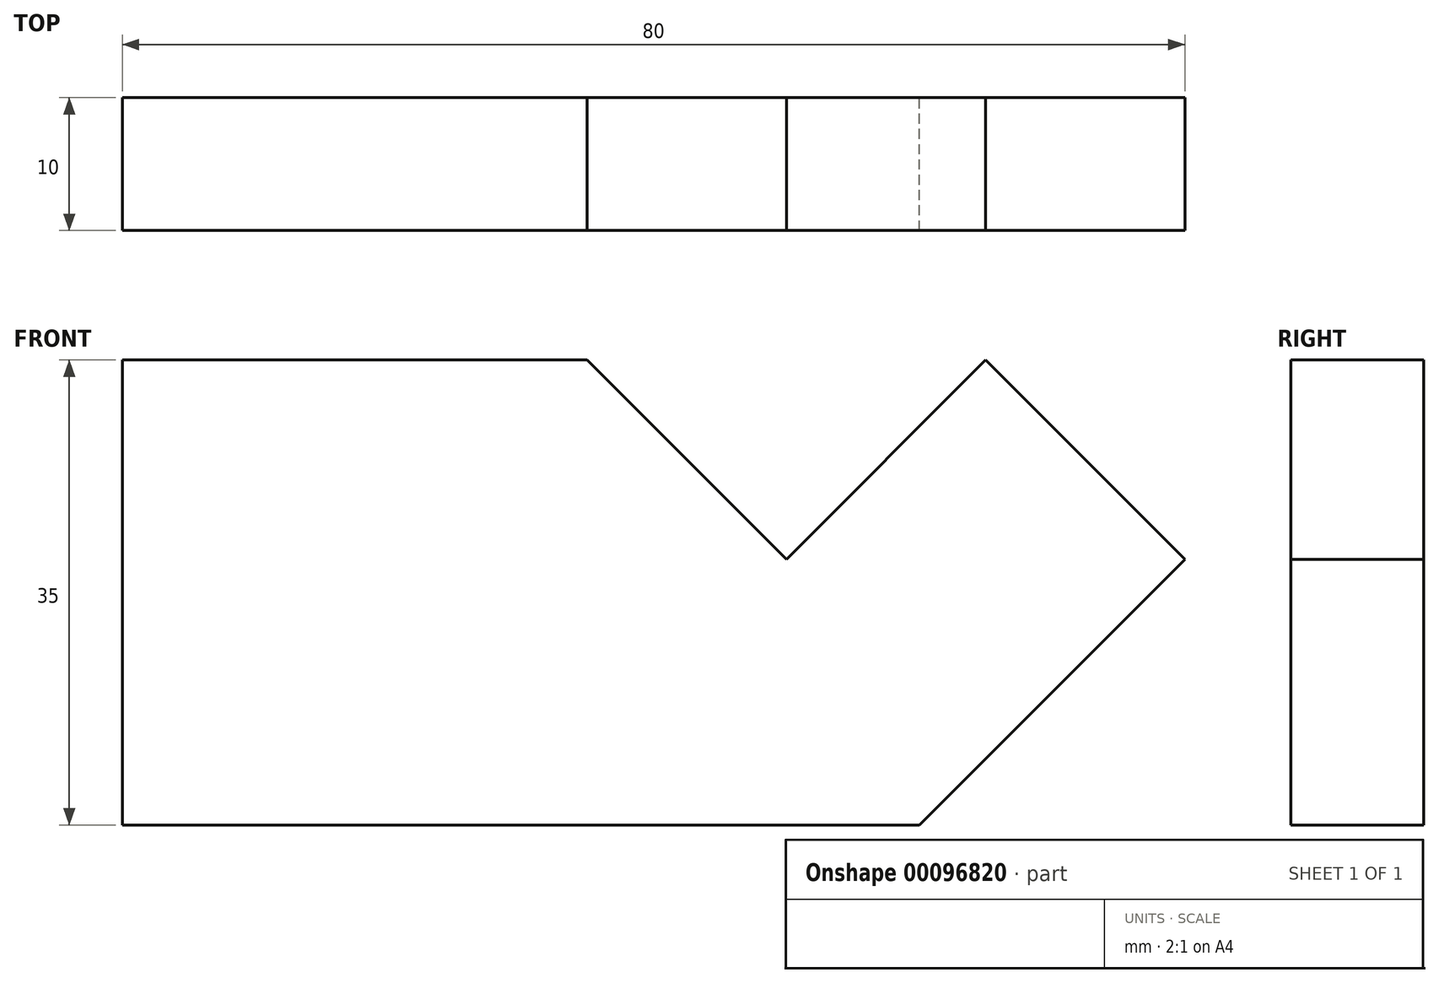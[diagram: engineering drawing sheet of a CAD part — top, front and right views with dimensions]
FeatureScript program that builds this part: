
annotation { "Feature Type Name" : "Feature", "Feature Type Description" : "" }
export const myFeature = defineFeature(function(context is Context, id is Id, definition is map)
    precondition{}
    {
        {
            var Q0;
            Q0=qCreatedBy(makeId("Front.planeOp"),FACE);
            var sketch = newSketch(context, id + "F0", { "sketchPlane" : qUnion([Q0])});
            skLineSegment(sketch, "E0", {"start": v(0, 0) * mm, "end": v(60, 0) * mm});
            skLineSegment(sketch, "E1", {"start": v(60, 0) * mm, "end": v(80, 20) * mm});
            skLineSegment(sketch, "E2", {"start": v(80, 20) * mm, "end": v(65, 35) * mm});
            skLineSegment(sketch, "E3", {"start": v(65, 35) * mm, "end": v(50, 20) * mm});
            skLineSegment(sketch, "E4", {"start": v(50, 20) * mm, "end": v(35, 35) * mm});
            skLineSegment(sketch, "E5", {"start": v(35, 35) * mm, "end": v(0, 35) * mm});
            skLineSegment(sketch, "E6", {"start": v(0, 35) * mm, "end": v(0, 0) * mm});
            skSolve(sketch);
        }
        {
            var Q0;
            Q0=makeQuery(id+"F0.imprint","IMPRINT",FACE,{"disambiguationData":[TD([[makeQuery(id+"F0.imprint","IMPRINT",EDGE,{"derivedFrom":sQuery(id+"F0.wireOp",EDGE,"E0")}),1.0]])]});
            extrude(context, id + "F1", {"entities" : qUnion([Q0]), "depth" : 10 * mm});
        }
    });
